FCSTD DOCUMENT  (FreeCAD 0.19R24291 (Git))
Label: frame_spring03
License: All rights reserved
LicenseURL: http://en.wikipedia.org/wiki/All_rights_reserved
objects: Sketcher::SketchObject×9, Part::Sweep×6, Part::FeaturePython×5, Part::Box×3, Part::Chamfer×2, Part::Cut×2, Spreadsheet::Sheet×1, Part::Helix×1, Part::Line×1, Part::Circle×1, Part::Fillet×1, Part::MultiCommon×1
note: 32 computed .brp shape members not serialized (recipe doc carries the construction recipe); baked Part::Feature solids carry a one-line shape summary decoded from their .brp

FEATURE [Spreadsheet::Sheet] Spreadsheet
  cells = B2=Frame; C2=spring ; B4=blank; C5=ln; D5(bln_ln)=26; C6=w; D6(bln_w)=30; C7=h; D7(bln_h)=15; C8=shift; D8(bln_sh)=42.5; B9=slope; C9=ln; D9(bln_sl_ln)=6.5; C10=h; D10(bln_sl_h)=1.7
FEATURE [Part::Box] Box  label="Cube"
  AttacherType = Attacher::AttachEngine3D
  Height = 15
  Length = 26
  Width = 30
  expr: Height = Spreadsheet.bln_h
  expr: Width = Spreadsheet.bln_w
  expr: Length = Spreadsheet.bln_ln
FEATURE [Part::Helix] Helix
  Angle = 0
  AttacherType = Attacher::AttachEngine3D
  Height = 13
  LocalCoord = 0
  Pitch = 7
  Radius = 16
  Style = 1
FEATURE [Part::Line] Line
  AttacherType = Attacher::AttachEngine3D
  X1 = 0
  X2 = 16
  Y1 = 0
  Y2 = 0
  Z1 = 0
  Z2 = 0
FEATURE [Part::Sweep] Sweep
  Frenet = true
  Placement = pos=(6.5,15,9) rot=(0.694747,-0.186157,0.694747;3.50969rad)
  Sections = -> [Line]
  Solid = false
  Spine = -> Helix [Edge1,Edge2]
  Transition = 1
FEATURE [Part::Circle] Circle
  Angle0 = 0
  Angle1 = 360
  AttacherType = Attacher::AttachEngine3D
  Placement = pos=(19.5,17.5,15) rot=(-0.983106,-0.129428,0.129428;1.58783rad)
  Radius = 0.5
FEATURE [Part::Box] Box001  label="cut1"
  AttacherType = Attacher::AttachEngine3D
  Height = 7
  Length = 6.5
  Placement = pos=(0,0,16.5) rot=(0,0,1;0rad)
  Width = 30
FEATURE [Part::Chamfer] Chamfer
  Base = -> Box001
  Edges = 1 edges: [Edge4 r1=1.6 r2=6.4]
  Placement = pos=(19.5,0,-8.5) rot=(0,0,1;0rad)
FEATURE [Part::Cut] Cut
  Base = -> Box
  Tool = -> Chamfer
FEATURE [Part::Box] Box002  label="cut2"
  AttacherType = Attacher::AttachEngine3D
  Height = 7
  Length = 6.5
  Placement = pos=(0,0,16) rot=(0,0,1;0rad)
  Width = 30
FEATURE [Part::Chamfer] Chamfer001
  Base = -> Box002
  Edges = 1 edges: [Edge8 r1=1.6 r2=6.4]
  Placement = pos=(0,0,-8) rot=(0,0,1;0rad)
FEATURE [Part::Cut] Cut001
  Base = -> Cut
  Tool = -> Chamfer001
FEATURE [Part::Fillet] Fillet
  Base = -> Cut001
  Edges = 4 edges r=7: [Edge9,Edge13,Edge20,Edge23]
FEATURE [Part::MultiCommon] Common
  Shapes = -> [Sweep,Fillet]
FEATURE [Part::Sweep] Sweep001
  Frenet = false
  Sections = -> [Circle]
  Solid = true
  Spine = -> Common [Edge16,Edge17,Edge18,Edge19,Edge20,Edge21,Edge22,Edge23,Edge24,Edge3,Edge4,Edge5,Edge6,Edge7,Edge8,Edge9,Edge10,Edge11]
  Transition = 1
FEATURE [Sketcher::SketchObject] Sketch
  ExternalGeometry = -> [Box]
  FullyConstrained = false
  MapMode = 5
  Placement = pos=(0,0,15) rot=(0,0,1;0rad)
  Support = -> [Box]
  sketch-geometry (1):
    g0: LineSegment StartX=-8.55419 StartY=15 StartZ=0 EndX=30.4099 EndY=15 EndZ=0
  constraints (1):
    c: Symmetric(g-3,g-3,g0)
FEATURE [Sketcher::SketchObject] Sketch005
  FullyConstrained = false
  MapMode = 5
  Placement = pos=(6.5,0,0) rot=(0.57735,-0.57735,-0.57735;2.0944rad)
  Support = -> [Fillet]
  sketch-geometry (19):
    g0-g9: Circle x10 (B-spline internal-alignment scaffolding for g10; pole/knot coordinates omitted)
    g10: BSplineCurve PolesCount=10 KnotsCount=8 Degree=3 IsPeriodic=0
    g11-g18: GeomPoint x8 (B-spline internal-alignment scaffolding for g10; pole/knot coordinates omitted)
  constraints (17):
    c: Weight(g0) = 1
    c: Equal(g0,g1)
    c: Equal(g0,g2)
    c: Equal(g0,g3)
    c: PointOnObject(g3,g2)
    c: Equal(g0,g4)
    c: PointOnObject(g4,g3)
    c: Equal(g0,g5)
    c: PointOnObject(g5,g4)
    c: Equal(g0,g6)
    c: PointOnObject(g6,g5)
    c: Equal(g0,g7)
    c: Equal(g0,g8)
    c: Equal(g0,g9)
    c: PointOnObject(g10,g7)
    c: InternalAlignment(g0-g9 -> g10) x10
    c: InternalAlignment(g11-g18 -> g10) x8
FEATURE [Sketcher::SketchObject] Sketch006
  FullyConstrained = false
  MapMode = 5
  Placement = pos=(-1.75446,8.51031,-0.716849) rot=(-0.068635,0.734449,0.675185;3.29063rad)
  Support = -> [Sweep001]
  sketch-geometry (1):
    g0: Circle CenterX=-8.4443 CenterY=15.9356 CenterZ=0 NormalX=0 NormalY=0 NormalZ=1 AngleXU=0 Radius=0.5
  constraints (1):
    c: Radius(g0) = 0.5
FEATURE [Part::Sweep] Sweep004
  Frenet = false
  Sections = -> [Sketch006]
  Solid = true
  Spine = -> Sketch005 [Edge1]
  Transition = 1
FEATURE [Sketcher::SketchObject] Sketch007
  FullyConstrained = false
  MapMode = 5
  Placement = pos=(-1.87647,-2e-16,7.50588) rot=(0,-1,0;0.244979rad)
  Support = -> [Fillet]
  sketch-geometry (21):
    g0-g10: Circle x11 (B-spline internal-alignment scaffolding for g11; pole/knot coordinates omitted)
    g11: BSplineCurve PolesCount=11 KnotsCount=9 Degree=3 IsPeriodic=0
    g12-g20: GeomPoint x9 (B-spline internal-alignment scaffolding for g11; pole/knot coordinates omitted)
  constraints (10):
    c: Weight(g0) = 1
    c: Equal(g0, g1-g4) x4
    c: PointOnObject(g4,g3)
    c: Equal(g0,g5)
    c: PointOnObject(g5,g4)
    c: Equal(g0,g6)
    c: PointOnObject(g6,g5)
    c: Equal(g0, g7-g10) x4
    c: InternalAlignment(g0-g10 -> g11) x11
    c: InternalAlignment(g12-g20 -> g11) x9
FEATURE [Sketcher::SketchObject] Sketch008
  FullyConstrained = false
  MapMode = 5
  Placement = pos=(-2.81371,13.1622,3.78911) rot=(-0.080949,0.599424,0.796328;3.26331rad)
  Support = -> [Sweep004]
  sketch-geometry (1):
    g0: Circle CenterX=-9.53976 CenterY=5.5728 CenterZ=0 NormalX=0 NormalY=0 NormalZ=1 AngleXU=0 Radius=0.5
  constraints (1):
    c: Radius(g0) = 0.5
FEATURE [Part::Sweep] Sweep005
  Frenet = false
  Sections = -> [Sketch008]
  Solid = true
  Spine = -> Sketch007 [Edge1]
  Transition = 1
FEATURE [Sketcher::SketchObject] Sketch009
  FullyConstrained = false
  MapMode = 5
  Placement = pos=(19.5,0,0) rot=(0.57735,0.57735,0.57735;2.0944rad)
  Support = -> [Fillet]
  sketch-geometry (19):
    g0-g9: Circle x10 (B-spline internal-alignment scaffolding for g10; pole/knot coordinates omitted)
    g10: BSplineCurve PolesCount=10 KnotsCount=8 Degree=3 IsPeriodic=0
    g11-g18: GeomPoint x8 (B-spline internal-alignment scaffolding for g10; pole/knot coordinates omitted)
  constraints (8):
    c: Weight(g0) = 1
    c: Equal(g0,g1)
    c: Equal(g0,g2)
    c: Equal(g0,g3)
    c: PointOnObject(g3,g1)
    c: Equal(g0, g4-g9) x6
    c: InternalAlignment(g0-g9 -> g10) x10
    c: InternalAlignment(g11-g18 -> g10) x8
FEATURE [Sketcher::SketchObject] Sketch010
  FullyConstrained = false
  MapMode = 5
  Placement = pos=(-3.0455,11.2533,-1.81e-14) rot=(0.982786,0.130636,0.130636;1.58816rad)
  Support = -> [Sweep001]
  sketch-geometry (1):
    g0: Circle CenterX=23.3818 CenterY=15.0007 CenterZ=0 NormalX=0 NormalY=0 NormalZ=1 AngleXU=0 Radius=0.5
  constraints (1):
    c: Radius(g0) = 0.5
FEATURE [Part::Sweep] Sweep006
  Frenet = false
  Sections = -> [Sketch010]
  Solid = true
  Spine = -> Sketch009 [Edge1]
  Transition = 1
FEATURE [Sketcher::SketchObject] Sketch011
  FullyConstrained = false
  MapMode = 5
  Placement = pos=(3.40588,-4e-16,13.6235) rot=(0,1,0;0.244979rad)
  Support = -> [Fillet]
  sketch-geometry (21):
    g0-g10: Circle x11 (B-spline internal-alignment scaffolding for g11; pole/knot coordinates omitted)
    g11: BSplineCurve PolesCount=11 KnotsCount=9 Degree=3 IsPeriodic=0
    g12-g20: GeomPoint x9 (B-spline internal-alignment scaffolding for g11; pole/knot coordinates omitted)
  constraints (8):
    c: Weight(g0) = 1
    c: Equal(g0, g1-g4) x4
    c: PointOnObject(g4,g3)
    c: Equal(g0, g5-g9) x5
    c: PointOnObject(g9,g8)
    c: Equal(g0,g10)
    c: InternalAlignment(g0-g10 -> g11) x11
    c: InternalAlignment(g12-g20 -> g11) x9
FEATURE [Sketcher::SketchObject] Sketch012
  FullyConstrained = false
  MapMode = 5
  Placement = pos=(-2.66332,9.84096,0.0620639) rot=(0.982891,0.129829,0.13065;1.59436rad)
  Support = -> [Sweep006]
  sketch-geometry (1):
    g0: Circle CenterX=22.9875 CenterY=9.50393 CenterZ=0 NormalX=0 NormalY=0 NormalZ=1 AngleXU=0 Radius=0.5
  constraints (1):
    c: Radius(g0) = 0.5
FEATURE [Part::Sweep] Sweep007
  Frenet = false
  Sections = -> [Sketch012]
  Solid = true
  Spine = -> Sketch011 [Edge1]
  Transition = 1
FEATURE [Part::FeaturePython] Array  # Draft array (typed FeaturePython)
  Angle = 360
  ArrayType = 1
  Axis = (0,1,0)
  Base = -> Sweep001
  Center = (13,0,-39.5)
  Count = 12
  ExpandArray = false
  Fuse = true
  IntervalAxis = (0,0,0)
  IntervalX = (50,0,0)
  IntervalY = (0,50,0)
  IntervalZ = (0,0,50)
  NumberCircles = 3
  NumberPolar = 12
  NumberX = 2
  NumberY = 2
  NumberZ = 1
  PlacementList = 12 placements: [(0,0,0),(21.4917,0,1.208),(40.708,0,-8.49167),(52.5,0,-26.5),(53.708,0,-47.9917),(44.0083,0,-67.208),(26,0,-79),(4.50833,0,-80.208),(-14.708,0,-70.5083),(-26.5,0,-52.5),(-27.708,0,-31.0083),(-18.0083,0,-11.792)]
  RadialDistance = 50
  ScaleList = (12) [(1,1,1),(1,1,1),(1,1,1),(1,1,1),(1,1,1),(1,1,1),(1,1,1),(1,1,1),(1,1,1),(1,1,1),(1,1,1),(1,1,1)]
  Symmetry = 1
  TangentialDistance = 25
FEATURE [Part::FeaturePython] Array001  # Draft array (typed FeaturePython)
  Angle = 360
  ArrayType = 1
  Axis = (0,1,0)
  Base = -> Sweep005
  Center = (13,0,-39.5)
  Count = 12
  ExpandArray = false
  Fuse = true
  IntervalAxis = (0,0,0)
  IntervalX = (50,0,0)
  IntervalY = (0,50,0)
  IntervalZ = (0,0,50)
  NumberCircles = 3
  NumberPolar = 12
  NumberX = 2
  NumberY = 2
  NumberZ = 1
  PlacementList = <same value as first occurrence — deduplicated (x5 in doc)>
  RadialDistance = 50
  ScaleList = (12) [(1,1,1),(1,1,1),(1,1,1),(1,1,1),(1,1,1),(1,1,1),(1,1,1),(1,1,1),(1,1,1),(1,1,1),(1,1,1),(1,1,1)]
  Symmetry = 1
  TangentialDistance = 25
FEATURE [Part::FeaturePython] Array002  # Draft array (typed FeaturePython)
  Angle = 360
  ArrayType = 1
  Axis = (0,1,0)
  Base = -> Sweep006
  Center = (13,0,-39.5)
  Count = 12
  ExpandArray = false
  Fuse = true
  IntervalAxis = (0,0,0)
  IntervalX = (50,0,0)
  IntervalY = (0,50,0)
  IntervalZ = (0,0,50)
  NumberCircles = 3
  NumberPolar = 12
  NumberX = 2
  NumberY = 2
  NumberZ = 1
  PlacementList = <same value as first occurrence — deduplicated (x5 in doc)>
  RadialDistance = 50
  ScaleList = (12) [(1,1,1),(1,1,1),(1,1,1),(1,1,1),(1,1,1),(1,1,1),(1,1,1),(1,1,1),(1,1,1),(1,1,1),(1,1,1),(1,1,1)]
  Symmetry = 1
  TangentialDistance = 25
FEATURE [Part::FeaturePython] Array003  # Draft array (typed FeaturePython)
  Angle = 360
  ArrayType = 1
  Axis = (0,1,0)
  Base = -> Sweep004
  Center = (13,0,-39.5)
  Count = 12
  ExpandArray = false
  Fuse = true
  IntervalAxis = (0,0,0)
  IntervalX = (50,0,0)
  IntervalY = (0,50,0)
  IntervalZ = (0,0,50)
  NumberCircles = 3
  NumberPolar = 12
  NumberX = 2
  NumberY = 2
  NumberZ = 1
  PlacementList = <same value as first occurrence — deduplicated (x5 in doc)>
  RadialDistance = 50
  ScaleList = (12) [(1,1,1),(1,1,1),(1,1,1),(1,1,1),(1,1,1),(1,1,1),(1,1,1),(1,1,1),(1,1,1),(1,1,1),(1,1,1),(1,1,1)]
  Symmetry = 1
  TangentialDistance = 25
FEATURE [Part::FeaturePython] Array004  # Draft array (typed FeaturePython)
  Angle = 360
  ArrayType = 1
  Axis = (0,1,0)
  Base = -> Sweep007
  Center = (13,0,-39.5)
  Count = 12
  ExpandArray = false
  Fuse = true
  IntervalAxis = (0,0,0)
  IntervalX = (50,0,0)
  IntervalY = (0,50,0)
  IntervalZ = (0,0,50)
  NumberCircles = 3
  NumberPolar = 12
  NumberX = 2
  NumberY = 2
  NumberZ = 1
  PlacementList = <same value as first occurrence — deduplicated (x5 in doc)>
  RadialDistance = 50
  ScaleList = (12) [(1,1,1),(1,1,1),(1,1,1),(1,1,1),(1,1,1),(1,1,1),(1,1,1),(1,1,1),(1,1,1),(1,1,1),(1,1,1),(1,1,1)]
  Symmetry = 1
  TangentialDistance = 25
